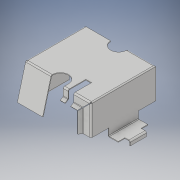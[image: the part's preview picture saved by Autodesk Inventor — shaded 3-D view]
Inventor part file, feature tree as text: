
AUTODESK INVENTOR PART (.ipt)
format: ipt  version: 2019 (Build 230136000, 136)  size: 632,832 bytes
history: native  units: mm
features: sheet_metal_op x15, sketch x15, delete_face x5, other x1
ambient origin geometry x8: Origin, YZ Plane, XZ Plane, XY Plane, X Axis, Y Axis, Z Axis, Center Point
bodies: Solid1 (feature_tree)
feature tree (36):
  sheet_metal_op  "Face1"
  sheet_metal_op  "Fold1"
  sheet_metal_op  "Fold2"
  sheet_metal_op  "Fold6"
  sheet_metal_op  "Fold7"
  sheet_metal_op  "Fold9"
  sheet_metal_op  "Fold10"
  sheet_metal_op  "Fold11"
  sheet_metal_op  "Fold12"
  sheet_metal_op  "Fold13"
  sheet_metal_op  "Fold14"
  sheet_metal_op  "Fold15"
  sheet_metal_op  "Fold16"
  sheet_metal_op  "Fold17"
  sheet_metal_op  "Fold18"
  delete_face  "Delete Face3"
  delete_face  "Delete Face4"
  delete_face  "Delete Face5"
  delete_face  "Delete Face9"
  delete_face  "Delete Face10"
  sketch  "Sketch1"  dims[d0=30.0mm]
  other  "Plate1"
  sketch  "Sketch2"  dims[d1=17.5mm]
  sketch  "Sketch3"  dims[d2=7.0mm]
  sketch  "Sketch7"  dims[d3=9.0mm]
  sketch  "Sketch8"  dims[d4=17.0mm]
  sketch  "Sketch12"  dims[d5=7.0mm]
  sketch  "Sketch13"  dims[d6=30.0mm]
  sketch  "Sketch14"  dims[d7=19.0mm]
  sketch  "Sketch15"  dims[d9=90.0deg]
  sketch  "Sketch16"  dims[d10=12.5mm]
  sketch  "Sketch17"  dims[d11=5.0mm]
  sketch  "Sketch18"  dims[d12=6.0mm]
  sketch  "Sketch19"  dims[d13=5.0mm]
  sketch  "Sketch20"  dims[d14=17.0mm]
  sketch  "Sketch21"  dims[d16=26.5mm d17=33.0mm d18=75.0deg d19=22.0mm d20=18.0mm d21=17.0mm d23=0.75mm d24=0.75mm d25=0.375mm d26=1.5mm d27=0.75mm d28=90.0deg d29=0.75mm d30=0.75mm d31=0.375mm d32=1.5mm d33=0.75mm d34=75.0deg d35=0.75mm d54=4.0mm d55=0.75mm d56=0.375mm d57=1.5mm d58=0.75mm d59=90.0deg d60=0.75mm d61=7.5mm d62=0.75mm d63=0.375mm d64=1.5mm d65=0.75mm d66=90.0deg d67=0.75mm d70=91.0mm d78=0.75mm d79=0.375mm d80=1.5mm d81=0.75mm d82=90.0deg d83=0.3mm d84=4.0mm d85=0.75mm d86=0.375mm d87=1.5mm d88=0.75mm d89=10.304424mm d90=0.75mm d91=4.0mm d92=0.75mm d93=0.375mm d94=1.5mm d95=0.75mm d96=10.304424mm d97=0.75mm d98=0.75mm d99=0.375mm d100=1.5mm d101=0.75mm d102=90.0deg d103=0.75mm d105=90.0deg d106=0.75mm d107=0.375mm d108=1.5mm d109=0.75mm d110=90.0deg d111=0.75mm d112=11.0mm d113=0.75mm d114=0.375mm d115=1.5mm d116=0.75mm d117=90.0deg d118=0.75mm d119=4.0mm d120=0.75mm d121=0.375mm d122=1.5mm d123=0.75mm d124=10.304424mm d125=0.75mm d126=0.75mm d127=0.375mm d128=1.5mm d129=0.75mm d130=90.0deg d131=0.75mm d132=4.0mm d133=0.75mm d134=0.375mm d135=1.5mm d136=0.75mm d137=10.304424mm d138=0.75mm d139=0.75mm d140=0.375mm d141=1.5mm d142=0.75mm d143=90.0deg d144=0.75mm]
